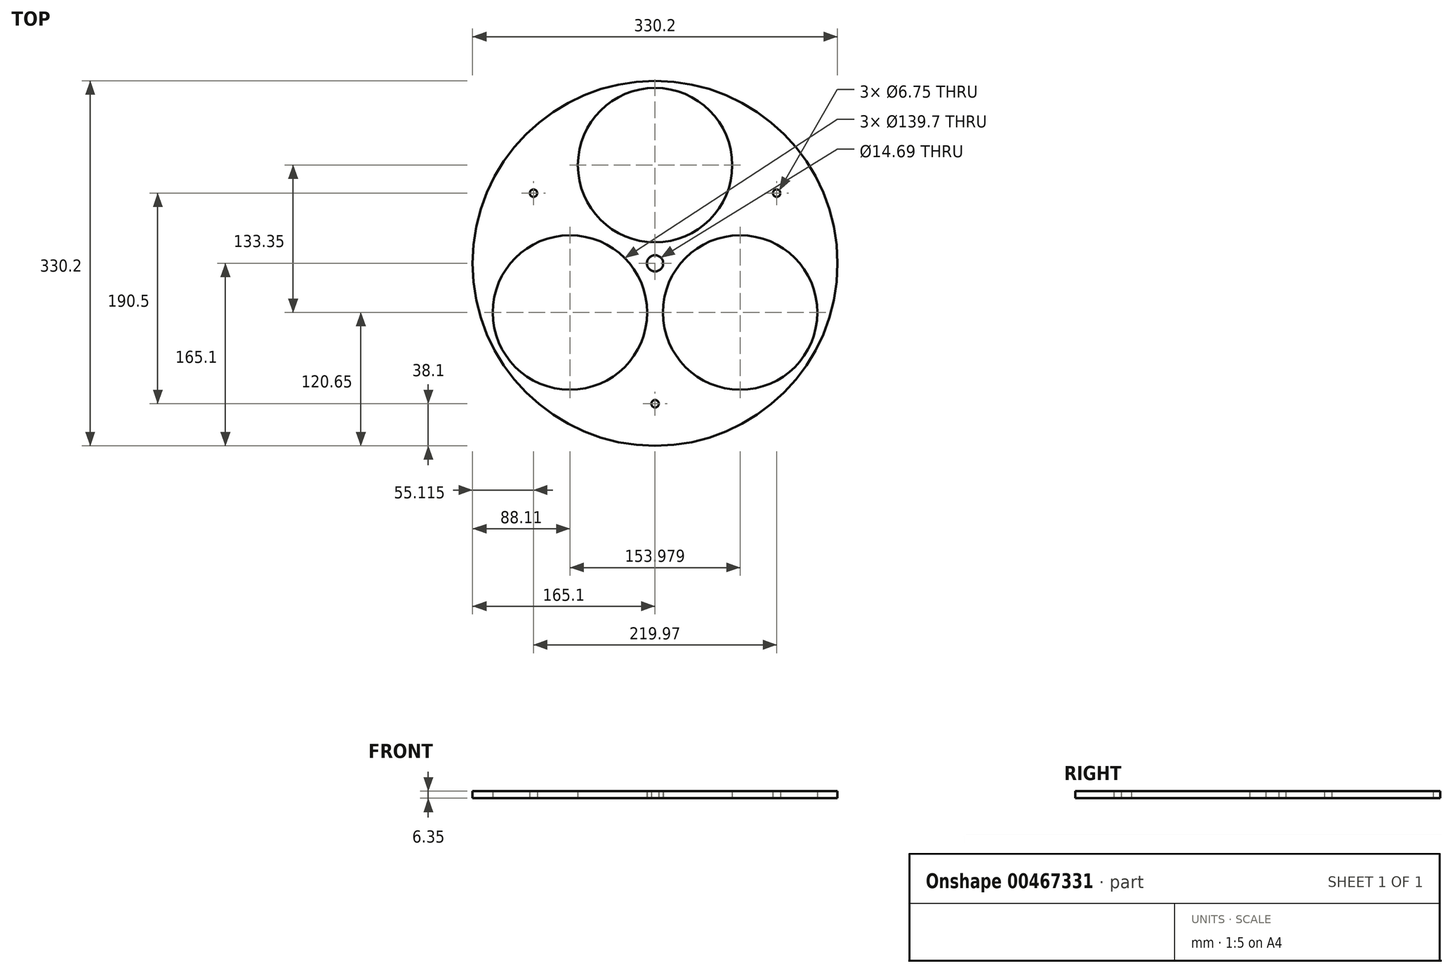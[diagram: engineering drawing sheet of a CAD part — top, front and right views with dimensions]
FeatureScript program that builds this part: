
annotation { "Feature Type Name" : "Feature", "Feature Type Description" : "" }
export const myFeature = defineFeature(function(context is Context, id is Id, definition is map)
    precondition{}
    {
        {
            var Q0;
            Q0=qCreatedBy(makeId("Top.planeOp"),FACE);
            var sketch = newSketch(context, id + "F0", { "sketchPlane" : qUnion([Q0])});
            skCircle(sketch, "E0", {"center": v(0, 0) * mm, "radius": 169.04 * mm});
            skCircle(sketch, "E1", {"center": v(0, 88.9) * mm, "radius": 69.85 * mm});
            skCircle(sketch, "E2.1.0", {"center": v(-76.99, -44.45) * mm, "radius": 69.85 * mm});
            skCircle(sketch, "E2.2.0", {"center": v(76.99, -44.45) * mm, "radius": 69.85 * mm});
            skCircle(sketch, "E3", {"center": v(0, 0) * mm, "radius": 7.34 * mm});
            skCircle(sketch, "E4", {"center": v(0, 0) * mm, "radius": 88.9 * mm, "construction": true});
            skCircle(sketch, "E5", {"center": v(0, 0) * mm, "radius": 168.28 * mm});
            skCircle(sketch, "E6", {"center": v(0, 0) * mm, "radius": 165.1 * mm});
            skCircle(sketch, "E7", {"center": v(0, 0) * mm, "radius": 127 * mm, "construction": true});
            skCircle(sketch, "E8", {"center": v(0, -127) * mm, "radius": 3.37 * mm});
            skCircle(sketch, "E9.1.0", {"center": v(109.99, 63.5) * mm, "radius": 3.37 * mm});
            skCircle(sketch, "E9.2.0", {"center": v(-109.99, 63.5) * mm, "radius": 3.37 * mm});
            skSolve(sketch);
        }
        {
            var Q0;
            Q0=makeQuery(id+"F0.imprint","IMPRINT",FACE,{"disambiguationData":[TD([[makeQuery(id+"F0.imprint","IMPRINT",EDGE,{"derivedFrom":sQuery(id+"F0.wireOp",EDGE,"E1")}),-1.0]])]});
            extrude(context, id + "F1", {"entities" : qUnion([Q0]), "depth" : 6.35 * mm});
        }
    });
